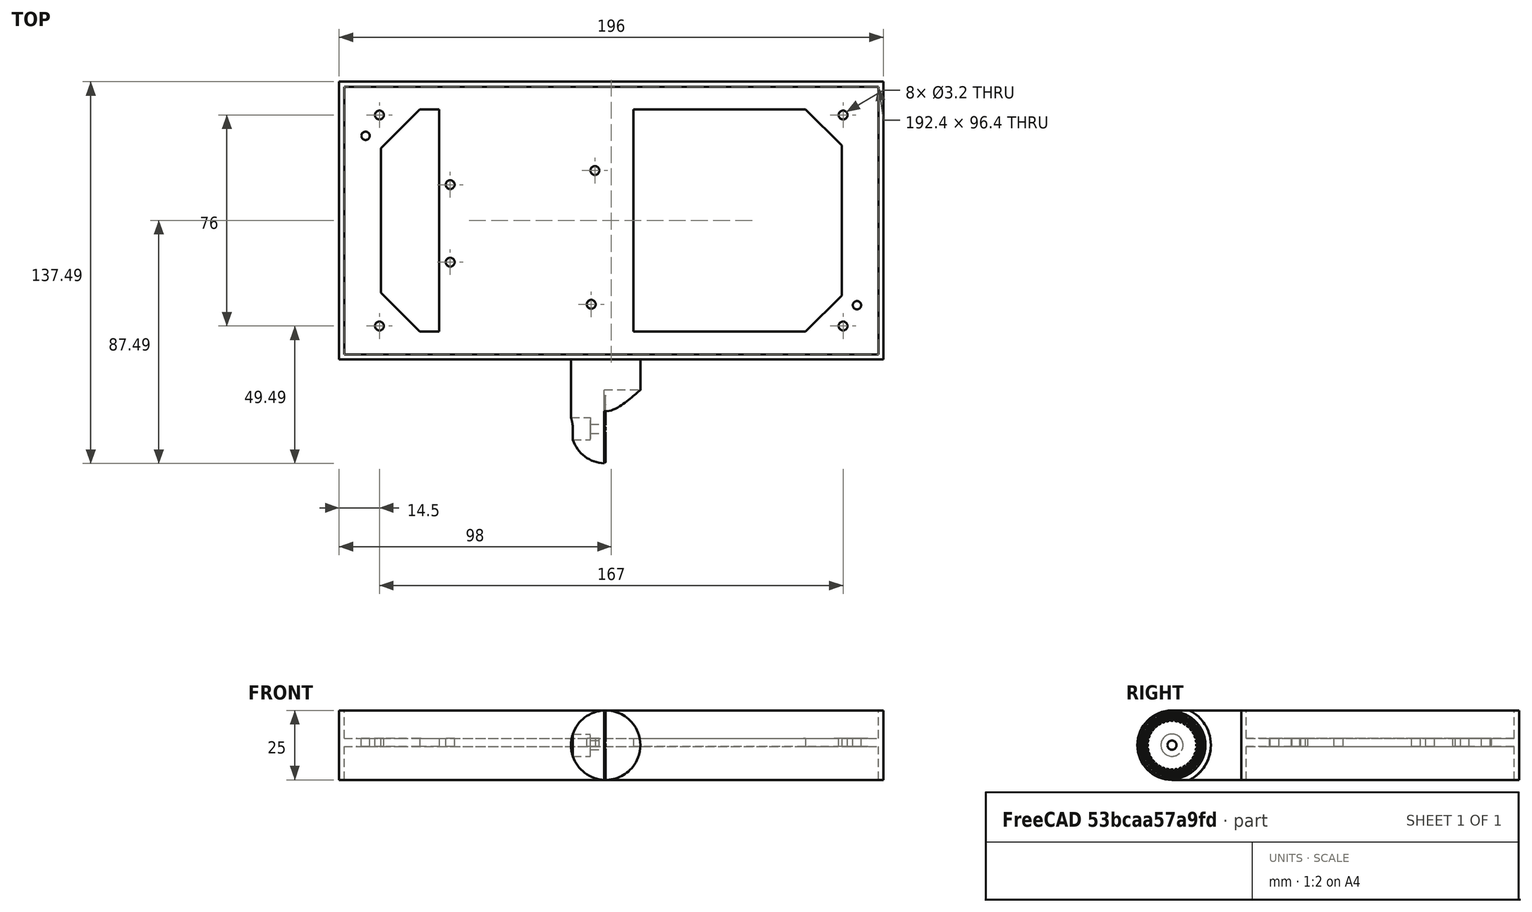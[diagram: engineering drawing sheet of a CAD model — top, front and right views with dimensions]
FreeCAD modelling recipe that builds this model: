
FCSTD DOCUMENT  (FreeCAD 0.18.1R)
Label: DisplayTop
License: All rights reserved
LicenseURL: http://en.wikipedia.org/wiki/All_rights_reserved
objects: Part::Cut×14, Part::Cylinder×14, Part::Box×9, Part::MultiFuse×5, Part::Sphere×1, Part::FeaturePython×1
note: 44 computed .brp shape members not serialized (recipe doc carries the construction recipe); baked Part::Feature solids carry a one-line shape summary decoded from their .brp

FEATURE [Part::Box] Box  label="Cube"
  AttacherType = Attacher::AttachEngine3D
  Height = 25
  Length = 196
  Width = 100
FEATURE [Part::Box] Box001  label="Cube001"
  AttacherType = Attacher::AttachEngine3D
  Height = 12
  Length = 192.4
  Placement = pos=(1.8,1.8,0) rot=(0,0,1;0rad)
  Width = 96.4
FEATURE [Part::Cut] Cut
  Base = -> Box
  Tool = -> Box001
FEATURE [Part::Box] Box002  label="Cube002"
  AttacherType = Attacher::AttachEngine3D
  Height = 25
  Length = 166
  Placement = pos=(15,10,0) rot=(0,0,1;0rad)
  Width = 80
FEATURE [Part::Cut] Cut001
  Base = -> Cut
  Tool = -> Box002
FEATURE [Part::Box] Box003  label="Cube003"
  AttacherType = Attacher::AttachEngine3D
  Height = 12
  Length = 192.4
  Placement = pos=(1.8,1.8,15) rot=(0,0,1;0rad)
  Width = 96.4
FEATURE [Part::Cut] Cut002
  Base = -> Cut001
  Tool = -> Box003
FEATURE [Part::Cylinder] Cylinder
  Angle = 360
  AttacherType = Attacher::AttachEngine3D
  Height = 25
  Placement = pos=(96,0,12.5) rot=(1,0,0;1.5708rad)
  Radius = 12.5
FEATURE [Part::Sphere] Sphere
  Angle1 = -90
  Angle2 = 90
  Angle3 = 360
  AttacherType = Attacher::AttachEngine3D
  Placement = pos=(96,-25,12.5) rot=(0,0,1;0rad)
  Radius = 12.5
FEATURE [Part::Cylinder] Cylinder001
  Angle = 360
  AttacherType = Attacher::AttachEngine3D
  Height = 13
  Placement = pos=(96,-25,12.5) rot=(0,1,0;1.5708rad)
  Radius = 14
FEATURE [Part::Cylinder] Cylinder002
  Angle = 360
  AttacherType = Attacher::AttachEngine3D
  Height = 25
  Placement = pos=(83,-25,12.5) rot=(0,1,0;1.5708rad)
  Radius = 1.65
FEATURE [Part::Cylinder] Cylinder003
  Angle = 360
  AttacherType = Attacher::AttachEngine3D
  Height = 7.5
  Placement = pos=(83.5,-25,12.5) rot=(0,1,0;1.5708rad)
  Radius = 4
FEATURE [Part::MultiFuse] Fusion
  Placement = pos=(-0.5,0,0) rot=(0,0,1;0rad)
  Shapes = -> [Cylinder001,Cylinder002,Cylinder003]
FEATURE [Part::MultiFuse] Fusion001
  Shapes = -> [Cylinder,Sphere]
FEATURE [Part::Cut] Cut003
  Base = -> Fusion001
  Tool = -> Fusion
FEATURE [Part::MultiFuse] Fusion002
  Shapes = -> [Cut003,Cut002]
FEATURE [Part::Cylinder] Cylinder004
  Angle = 360
  AttacherType = Attacher::AttachEngine3D
  Height = 10
  Placement = pos=(9.5,80.5,7) rot=(0,0,1;0rad)
  Radius = 1.5
FEATURE [Part::Cylinder] Cylinder005
  Angle = 360
  AttacherType = Attacher::AttachEngine3D
  Height = 10
  Placement = pos=(186.5,19.5,7) rot=(0,0,1;0rad)
  Radius = 1.5
FEATURE [Part::Box] Box004  label="Cube004"
  AttacherType = Attacher::AttachEngine3D
  Height = 3
  Length = 12
  Placement = pos=(21,1,12) rot=(0,0,1;0.785398rad)
  Width = 21
FEATURE [Part::Box] Box005  label="Cube005"
  AttacherType = Attacher::AttachEngine3D
  Height = 3
  Length = 12
  Placement = pos=(6,84,12) rot=(0,0,-1;0.785398rad)
  Width = 21
FEATURE [Part::Box] Box006  label="Cube006"
  AttacherType = Attacher::AttachEngine3D
  Height = 3
  Length = 12
  Placement = pos=(182,76,12) rot=(0,0,1;0.785398rad)
  Width = 21
FEATURE [Part::Box] Box007  label="Cube007"
  AttacherType = Attacher::AttachEngine3D
  Height = 3
  Length = 12
  Placement = pos=(167,9,12) rot=(0,0,-1;0.785398rad)
  Width = 21
FEATURE [Part::Cylinder] Cylinder006
  Angle = 360
  AttacherType = Attacher::AttachEngine3D
  Height = 25
  Placement = pos=(14.5,12,0) rot=(0,0,1;0rad)
  Radius = 1.6
FEATURE [Part::Cylinder] Cylinder007
  Angle = 360
  AttacherType = Attacher::AttachEngine3D
  Height = 25
  Placement = pos=(181.5,12,0) rot=(0,0,1;0rad)
  Radius = 1.6
FEATURE [Part::Cylinder] Cylinder008
  Angle = 360
  AttacherType = Attacher::AttachEngine3D
  Height = 25
  Placement = pos=(14.5,88,0) rot=(0,0,1;0rad)
  Radius = 1.6
FEATURE [Part::Cylinder] Cylinder009
  Angle = 360
  AttacherType = Attacher::AttachEngine3D
  Height = 25
  Placement = pos=(181.5,88,0) rot=(0,0,1;0rad)
  Radius = 1.6
FEATURE [Part::Box] Box008  label="Cube008"
  AttacherType = Attacher::AttachEngine3D
  Height = 3
  Length = 70
  Placement = pos=(36,2,12) rot=(0,0,1;0rad)
  Width = 96
FEATURE [Part::Cylinder] Cylinder010
  Angle = 360
  AttacherType = Attacher::AttachEngine3D
  Height = 25
  Placement = pos=(90.8,19.8,0) rot=(0,0,1;0rad)
  Radius = 1.6
FEATURE [Part::Cylinder] Cylinder011
  Angle = 360
  AttacherType = Attacher::AttachEngine3D
  Height = 25
  Placement = pos=(92.1,68,0) rot=(0,0,1;0rad)
  Radius = 1.6
FEATURE [Part::Cylinder] Cylinder012
  Angle = 360
  AttacherType = Attacher::AttachEngine3D
  Height = 25
  Placement = pos=(40,35,0) rot=(0,0,1;0rad)
  Radius = 1.6
FEATURE [Part::Cylinder] Cylinder013
  Angle = 360
  AttacherType = Attacher::AttachEngine3D
  Height = 25
  Placement = pos=(40,62.9,0) rot=(0,0,1;0rad)
  Radius = 1.6
FEATURE [Part::MultiFuse] Fusion003
  Shapes = -> [Fusion002,Box004,Box005,Box006,Box007,Box008]
FEATURE [Part::Cut] Cut004
  Base = -> Fusion003
  Tool = -> Cylinder004
FEATURE [Part::Cut] Cut005
  Base = -> Cut004
  Tool = -> Cylinder005
FEATURE [Part::Cut] Cut006
  Base = -> Cut005
  Tool = -> Cylinder006
FEATURE [Part::Cut] Cut007
  Base = -> Cut006
  Tool = -> Cylinder007
FEATURE [Part::Cut] Cut008
  Base = -> Cut007
  Tool = -> Cylinder008
FEATURE [Part::Cut] Cut009
  Base = -> Cut008
  Tool = -> Cylinder009
FEATURE [Part::Cut] Cut010
  Base = -> Cut009
  Tool = -> Cylinder010
FEATURE [Part::Cut] Cut011
  Base = -> Cut010
  Tool = -> Cylinder011
FEATURE [Part::Cut] Cut012
  Base = -> Cut011
  Tool = -> Cylinder012
FEATURE [Part::Cut] Cut013
  Base = -> Cut012
  Tool = -> Cylinder013
FEATURE [Part::FeaturePython] CrownGear  # WARN: FeaturePython — macro-defined, semantics opaque (R4)
  Placement = pos=(95,-25,12.5) rot=(0,1,0;-1.5708rad)
  construct = true
  height = 2.5
  module = 0.5
  num_profiles = 4
  other_teeth = 36
  pressure_angle = 20
  teeth = 36
  thickness = 0.1
FEATURE [Part::MultiFuse] Fusion004
  Shapes = -> [Cut013,CrownGear]
